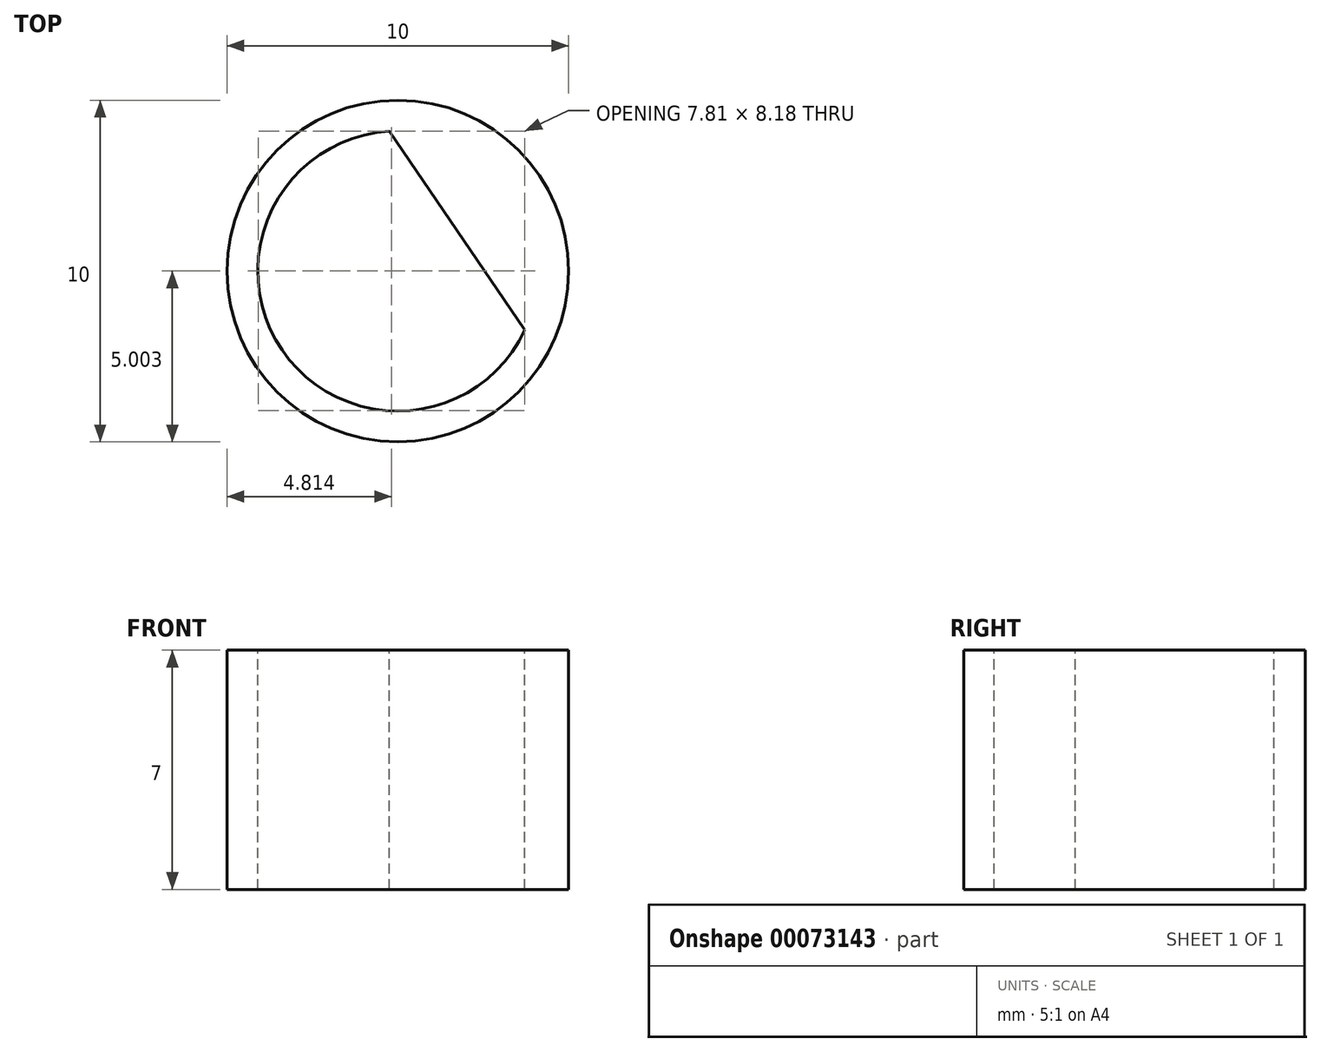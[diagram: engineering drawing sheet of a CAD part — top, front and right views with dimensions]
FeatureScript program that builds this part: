
annotation { "Feature Type Name" : "Feature", "Feature Type Description" : "" }
export const myFeature = defineFeature(function(context is Context, id is Id, definition is map)
    precondition{}
    {
        {
            var Q0;
            Q0=qCreatedBy(makeId("Top.planeOp"),FACE);
            var sketch = newSketch(context, id + "F0", { "sketchPlane" : qUnion([Q0])});
            skCircle(sketch, "E0", {"center": v(0, 0) * mm, "radius": 5 * mm});
            skSolve(sketch);
        }
        {
            var Q0;
            Q0 = qSketchRegion(id + "F0", true);
            extrude(context, id + "F1", {"entities" : qUnion([Q0]), "depth" : 7 * mm});
        }
        {
            var Q0;
            Q0=makeQuery(id+"F1.opExtrude","CAP_FACE",FACE,{"disambiguationData":[OSD([sQuery(id+"F0.wireOp",EDGE,"E0")])],"isStart":false});
            var sketch = newSketch(context, id + "F2", { "sketchPlane" : qUnion([Q0])});
            skCircle(sketch, "E1", {"center": v(0, 0) * mm, "radius": 4.1 * mm});
            skLineSegment(sketch, "E2", {"start": v(-3.39, -2.3) * mm, "end": v(1.74, 1.18) * mm});
            skLineSegment(sketch, "E3", {"start": v(-0.25, 4.1) * mm, "end": v(3.72, -1.73) * mm});
            skSolve(sketch);
        }
        {
            var Q0;
            {var subQ0=sQuery(id+"F2.wireOp",EDGE,"E2");Q0=makeQuery(id+"F2.imprint","IMPRINT",FACE,{"disambiguationData":[TD([[makeQuery(id+"F2.imprint","IMPRINT",EDGE,{"derivedFrom":subQ0}),1.0]])]});}
            var Q1;
            {var subQ0=sQuery(id+"F2.wireOp",EDGE,"E2");Q1=makeQuery(id+"F2.imprint","IMPRINT",FACE,{"disambiguationData":[TD([[makeQuery(id+"F2.imprint","IMPRINT",EDGE,{"derivedFrom":subQ0}),-1.0]])]});}
            extrude(context, id + "F3", {"entities" : qUnion([Q0, Q1]), "operationType" : NewBodyOperationType.REMOVE, "endBound" : BoundingType.THROUGH_ALL, "oppositeDirection" : true, "depth" : 25.4 * mm});
        }
    });
